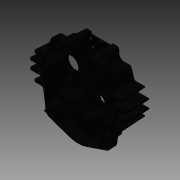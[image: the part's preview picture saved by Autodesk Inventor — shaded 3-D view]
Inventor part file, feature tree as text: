
AUTODESK INVENTOR PART (.ipt)
format: ipt  version: 2013 (Build 170138000, 138)  size: 3,713,024 bytes
history: native  units: in
note: dims shown in document units (in); Inventor stores cm internally (conversion verified against a paired STEP export)
features: projected_geometry x4, sketch x3, other x2, extrude x2, hole x1, imported_body x1
ambient origin geometry x8: Origin, YZ Plane, XZ Plane, XY Plane, X Axis, Y Axis, Z Axis, Center Point
feature tree (13):
  other  "Toughbox-mini_d01-5-12"
  other  "Toughbox-mini_d01-5-121"
  extrude  "Extrusion1"  Depth=1.25in
  hole  "Hole1"  [1 undecoded]
  extrude  "Extrusion2"  Depth=0.1875in
  imported_body  "Base1"
  sketch  "Sketch1"  dims[d0=1.125in d2=1.25in]
  sketch  "Sketch2"  dims[d3=0.3937in d4=0.0in d5=0.0787in]
  projected_geometry  "Projected Loop1"
  projected_geometry  "Projected Loop2"
  projected_geometry  "Projected Loop3"
  projected_geometry  "Projected Loop4"
  sketch  "Sketch3"  dims[d6=1.0in d9=0.1875in d10=0.75in d11=0.1875in d12=0.2362in d13=0.1575in d14=0.0787in d15=90.0deg d16=0.315in d17=0.8108in d18=0.375in d19=1.25in d22=0.3937in d23=0.0in d24=1.25in d26=0.0394in d27=0.0787in]
note: 1 required parameter value undecoded (feature->parameter linkage not recoverable at this tier; creation-order binding heuristic only, values carry confidence <= 0.55)
